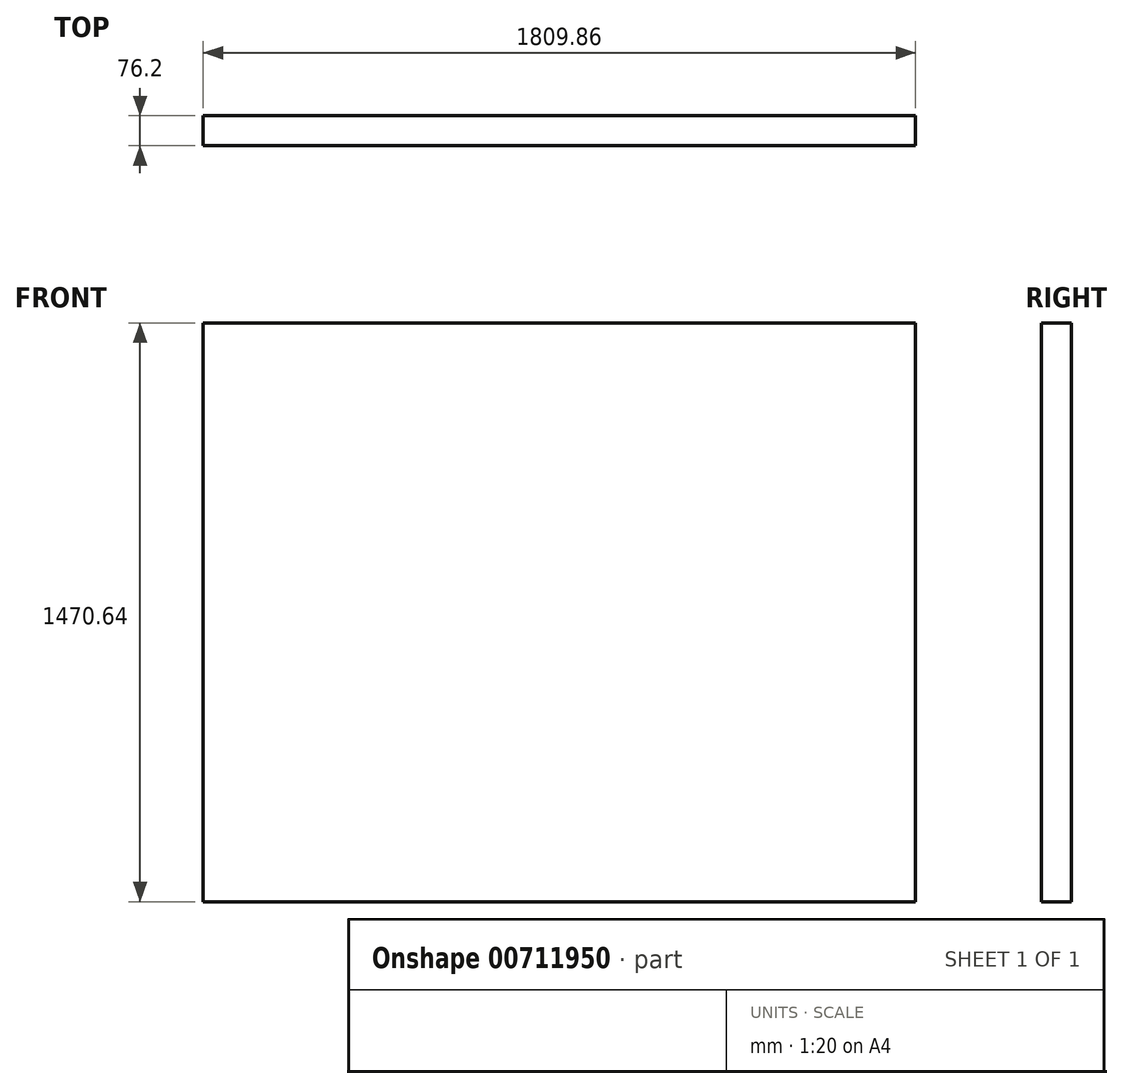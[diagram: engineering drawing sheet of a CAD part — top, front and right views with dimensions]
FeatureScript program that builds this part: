
annotation { "Feature Type Name" : "Feature", "Feature Type Description" : "" }
export const myFeature = defineFeature(function(context is Context, id is Id, definition is map)
    precondition{}
    {
        {
            var Q0;
            Q0=qCreatedBy(makeId("Front.planeOp"),FACE);
            var sketch = newSketch(context, id + "F0", { "sketchPlane" : qUnion([Q0])});
            skLineSegment(sketch, "E0.bottom", {"start": v(-904.93, 735.32) * mm, "end": v(904.93, 735.32) * mm});
            skLineSegment(sketch, "E0.top", {"start": v(-904.93, -735.32) * mm, "end": v(904.93, -735.32) * mm});
            skLineSegment(sketch, "E0.left", {"start": v(-904.93, 735.32) * mm, "end": v(-904.93, -735.32) * mm});
            skLineSegment(sketch, "E0.right", {"start": v(904.93, 735.32) * mm, "end": v(904.93, -735.32) * mm});
            skPoint(sketch, "E0.middle", {"position": v(0, 0) * mm});
            skCircle(sketch, "E1", {"center": v(-803.33, 0) * mm, "radius": 101.6 * mm});
            skSolve(sketch);
        }
        {
            var Q0;
            Q0 = qSketchRegion(id + "F0", true);
            extrude(context, id + "F1", {"entities" : qUnion([Q0]), "depth" : 76.2 * mm, "offsetDistance" : 25.4 * mm});
        }
    });
